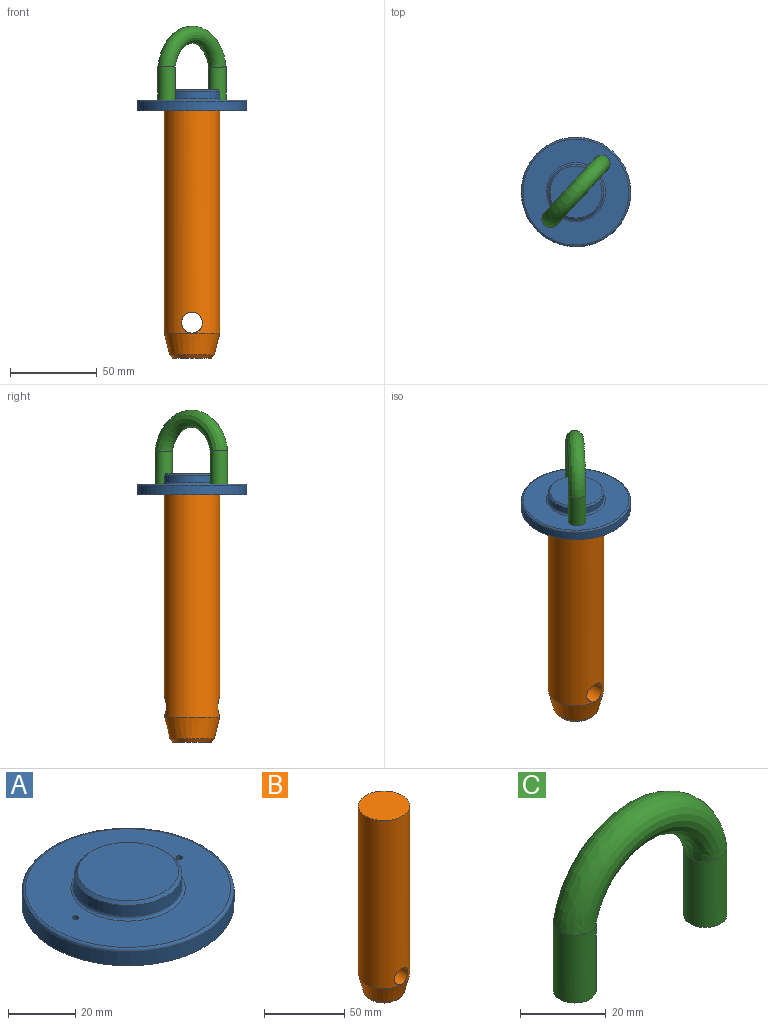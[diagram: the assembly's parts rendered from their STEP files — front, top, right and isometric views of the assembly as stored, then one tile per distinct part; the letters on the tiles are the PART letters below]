
ASSEMBLY  parts=3 mates=2
PART A: 12 faces, bbox 68.2x68.2x12 mm
  f0: cylinder r=31.5mm len=63mm, axis (0,0,-1), area 989.6mm2, adj f2,f7
  f1: plane 61x61mm, normal (0,0,1), area 2008.3mm2, adj f6,f7,f8,f10
  f2: plane 63x63mm, normal (0,0,-1), area 3117.2mm2, adj f0
  f3: cylinder r=16mm len=32mm, axis (0,0,1), area 402.1mm2, adj f5,f6
  f4: plane 30x30mm, normal (0,0,1), area 706.9mm2, adj f5
  f5: cone r=15mm half-angle=45deg, axis (0,0,-1), area 137.7mm2, adj f3,f4
  f6: torus R=17mm, axis (0,0,1), area 161.5mm2, adj f1,f3
  f7: torus R=30.5mm, axis (0,0,1), area 307.3mm2, adj f0,f1
  f8: cylinder r=1mm len=3.1mm, axis (0,0,1), area 19.5mm2, adj f1,f9
  f9: cone r=0mm half-angle=59deg, axis (0,0,1), area 3.7mm2, adj f8
  f10: cylinder r=1mm len=3.1mm, axis (0,0,1), area 19.5mm2, adj f1,f11
  f11: cone r=0mm half-angle=59deg, axis (0,0,1), area 3.7mm2, adj f10
PART B: 6 faces, bbox 32x32x142.5 mm
  f0: cylinder r=16mm len=128.2mm, axis (0,0,-1), area 12657.4mm2, adj f1,f2,f5
  f1: plane 32x32mm, normal (0,0,1), area 804.2mm2, adj f0
  f2: cone r=16mm half-angle=14.1deg, axis (0,0,1), area 1168.4mm2, adj f0,f4
  f3: plane 22.75x22.75mm, normal (0,0,-1), area 406.5mm2, adj f4
  f4: cone r=11.38mm half-angle=40.1deg, axis (0,0,1), area 174.2mm2, adj f2,f3
  f5: cylinder r=6mm len=32mm, axis (0,-1,0), area 1162.7mm2, adj f0
PART C: 5 faces, bbox 53.1x10x42.7 mm
  f0: plane 10x10mm, normal (0,0,-1), area 78.5mm2, adj f2
  f1: plane 10x10mm, normal (0,0,-1), area 78.5mm2, adj f4
  f2: cylinder r=5mm len=19.51mm, axis (0,0,-1), area 601.7mm2, adj f0,f3
  f3: bspline ~53.07x24.63mm, area 1946.1mm2, adj f2,f4
  f4: cylinder r=5mm len=19.51mm, axis (0,0,1), area 601.7mm2, adj f1,f3
PLACE A rot(axis=(0,0,1),47.4deg) t=(0.03,-0.05,71.13)mm
PLACE B t=(0.03,-0.05,0.03)mm fixed
PLACE C rot(axis=(0,0,1),47.4deg) t=(0.02,0.32,71.13)mm
MATE fastened A.f8 <-> C.f2  axis (0,0,1) through (14.62,16.17,77.13)mm
MATE revolute B.f0 <-> A.f0  axis (0,0,1) through (0.03,-0.05,71.13)mm
